# Revit family: Trap-WallMounted-Vitra-OriginSeries-A45157
name_source: partatom
category: Plumbing Fixtures
revit_build: Autodesk Revit 2017 (Build: 20160225_1515(x64)
units: mm (PartAtom-declared; Revit-internal decimal feet)

## family parameters
Cut with Voids When Loaded = No
Host = Face
OmniClass Number = 23.45.55.17
OmniClass Title = Mixing Faucets
Part Type = Normal
Room Calculation Point = No
Round Connector Dimension = Use Diameter
Shared = Yes

## types (1)
- Trap-FloorMounted-Vitra-OriginSeries-A45157
    Article No. (default) = A45157
    BIMobject category = Sanitary - Taps & Mixers
    CW Connection = Yes
    Coating Material = Vitra-Chrome
    Color = Chrome
    Connection Diameter (mm) = 0 mm  [stored 0 ft]
    Cost = 0 $
    Default Elevation = 850 mm  [stored 2.78871 ft]
    Depth(mm) = 195 mm  [stored 0.639764 ft]
    Description = Washbasin Siphon Set
    Design country = Turkey
    HW Connection = Yes
    Height(mm) = 575 mm
    IFC Classification = Sanitary Terminal
    Manufacturer = Vitra
    Manufacturer name = Vitra
    Masterformat 2014 Code = 22 13 16
    Masterformat 2014 Description = Sanitary Waste and Vent Piping
    Model = A45157
    MountingType = Wall Mounted
    NBS Referans Code = 31-76
    NBS Referans Description = Sanitary Dispensing And Disposal Units
    Nominal height = 0.000
    Nominal width = 0.000
    Number Of Connections = 3 mm  [stored 0.00984252 ft]
    OmniClass Code = 23-21 23 27
    OmniClass Description = Residential Waste Disposal Units
    Product SKU = A45157
    Product Type = Trap Monoblock Siphon Set
    Product certification = https://vitraglobal.com
    Product data url = https://www.vitra.com.tr
    Product family = Origin
    Product group = Origin Trap Monoblock Siphon Set
    UNSPSC Code = 301815
    UNSPSC Description = Sanitary ware
    URL = https://vitraglobal.com
    Uniclass 1.4 Code = L7218
    Uniclass 1.4 Description = Sanitary disposal units
    Uniclass 2.0 Code = PR-31-76
    Uniclass 2.0 Description = Sanitary Dispensing And Disposal Units
    Uniclass 2015 Code = Pr_60_45_90
    Uniclass 2015 Name = Wastewater and water mixer products
    Uniformat II Code = D2010
    Uniformat II Description = Plumbing Fixtures
    Warranty Period (Year) = 10 Years
    Waste Connection = Yes
    Weight Net (kg) = 0,450
    Width(mm) = 265 mm  [stored 0.869423 ft]
    Youtube = https://www.youtube.com

note: [stored X ft] marks values corroborated as IEEE doubles in the binary element streams (Revit-internal decimal feet)

## geometry (parser evidence)
native form markers: Sweep x3
no freeform markers — native parametric forms only
